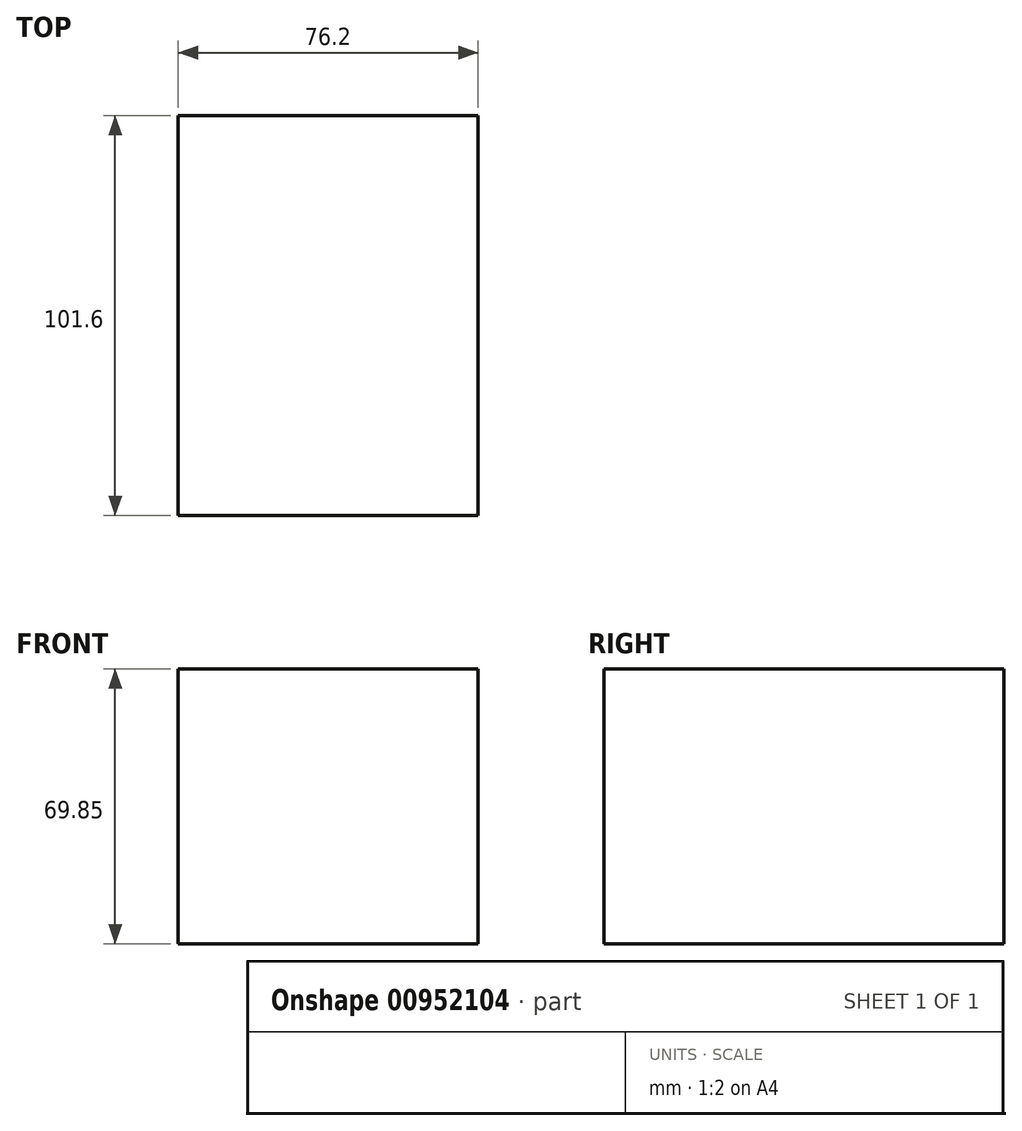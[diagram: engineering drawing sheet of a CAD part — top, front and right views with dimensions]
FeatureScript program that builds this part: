
annotation { "Feature Type Name" : "Feature", "Feature Type Description" : "" }
export const myFeature = defineFeature(function(context is Context, id is Id, definition is map)
    precondition{}
    {
        {
            var Q0;
            Q0=qCreatedBy(makeId("Top.planeOp"),FACE);
            var sketch = newSketch(context, id + "F0", { "sketchPlane" : qUnion([Q0])});
            skLineSegment(sketch, "E0.bottom", {"start": v(-37.25, 50.37) * mm, "end": v(38.95, 50.37) * mm});
            skLineSegment(sketch, "E0.top", {"start": v(-37.25, -51.23) * mm, "end": v(38.95, -51.23) * mm});
            skLineSegment(sketch, "E0.left", {"start": v(-37.25, 50.37) * mm, "end": v(-37.25, -51.23) * mm});
            skLineSegment(sketch, "E0.right", {"start": v(38.95, 50.37) * mm, "end": v(38.95, -51.23) * mm});
            skLineSegment(sketch, "E1", {"start": v(-37.25, 50.37) * mm, "end": v(38.95, -51.23) * mm, "construction": true});
            skSolve(sketch);
        }
        {
            var Q0;
            Q0 = qSketchRegion(id + "F0", true);
            extrude(context, id + "F1", {"entities" : qUnion([Q0]), "depth" : 69.85 * mm, "offsetDistance" : 25.4 * mm});
        }
    });
